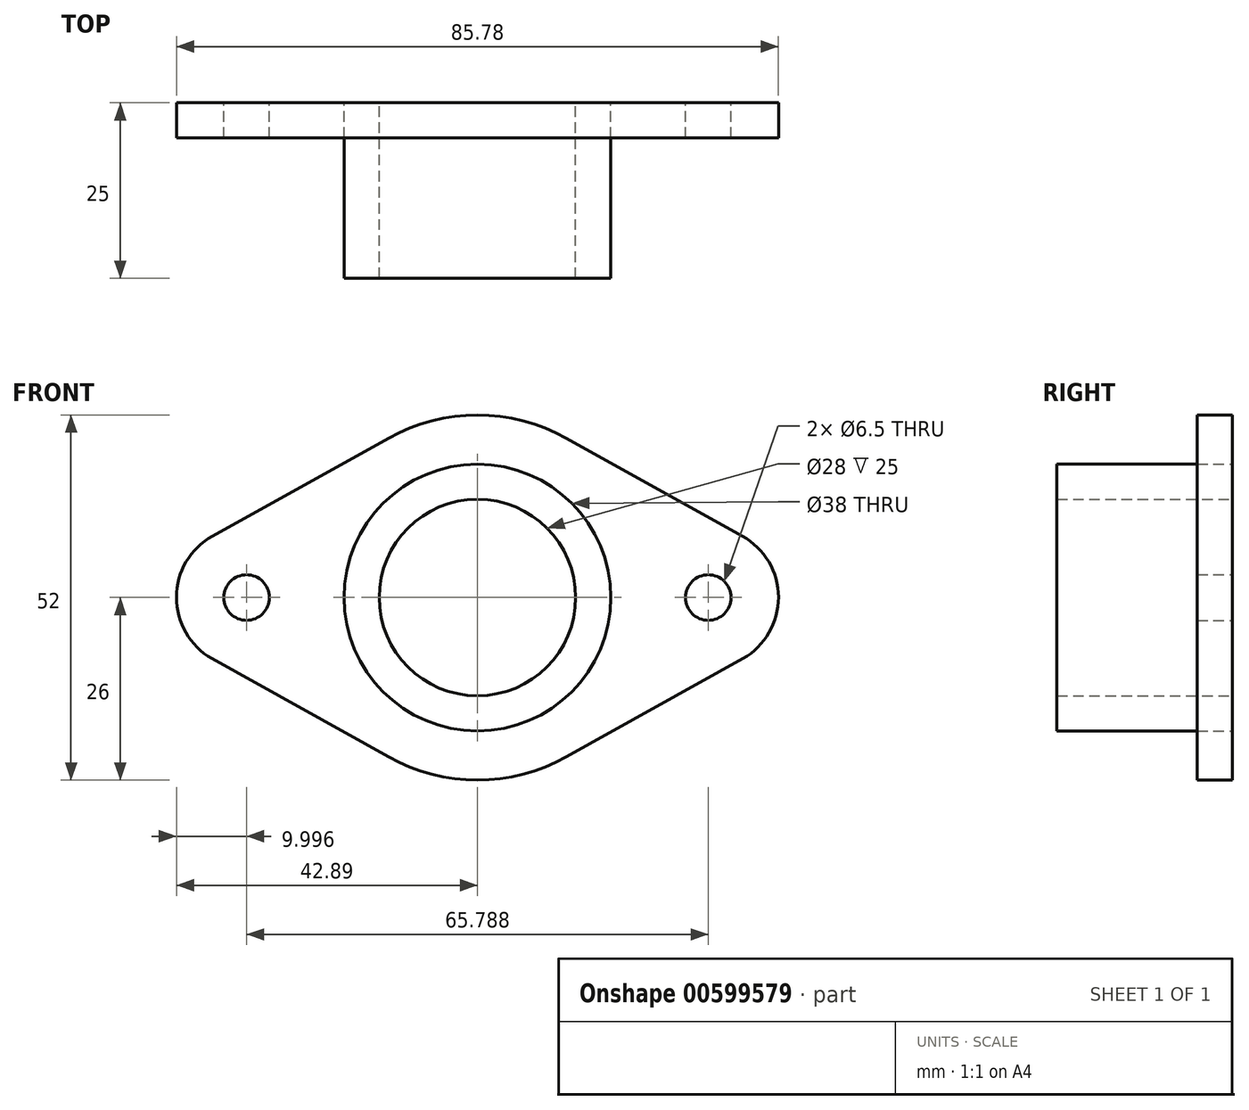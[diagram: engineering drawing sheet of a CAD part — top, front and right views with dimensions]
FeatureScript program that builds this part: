
annotation { "Feature Type Name" : "Feature", "Feature Type Description" : "" }
export const myFeature = defineFeature(function(context is Context, id is Id, definition is map)
    precondition{}
    {
        {
            var Q0;
            Q0=qCreatedBy(makeId("Front.planeOp"),FACE);
            var sketch = newSketch(context, id + "F0", { "sketchPlane" : qUnion([Q0])});
            skArc(sketch, "E0", {"start": v(0, 19) * mm, "mid": v(-19, 0) * mm, "end": v(0, -19) * mm});
            skCircle(sketch, "E1", {"center": v(-32.9, 0) * mm, "radius": 3.25 * mm});
            skLineSegment(sketch, "E2", {"start": v(0, 19) * mm, "end": v(0, 26) * mm});
            skLineSegment(sketch, "E3", {"start": v(0, -19) * mm, "end": v(0, -26) * mm});
            skArc(sketch, "E4", {"start": v(-37.76, 8.74) * mm, "mid": v(-42.9, 0.05) * mm, "end": v(-37.84, -8.7) * mm});
            skArc(sketch, "E5", {"start": v(0, 26) * mm, "mid": v(-6.53, 25.17) * mm, "end": v(-12.65, 22.72) * mm});
            skLineSegment(sketch, "E6", {"start": v(-12.65, 22.72) * mm, "end": v(-37.76, 8.74) * mm});
            skLineSegment(sketch, "E7", {"start": v(-37.84, -8.7) * mm, "end": v(-12.65, -22.72) * mm});
            skArc(sketch, "E8.trimOffspring", {"start": v(-12.65, -22.72) * mm, "mid": v(-6.53, -25.17) * mm, "end": v(0, -26) * mm});
            skLineSegment(sketch, "E9.MirrorCS", {"start": v(37.84, -8.7) * mm, "end": v(12.65, -22.72) * mm});
            skArc(sketch, "E10.MirrorCS", {"start": v(0, 26) * mm, "mid": v(6.53, 25.17) * mm, "end": v(12.65, 22.72) * mm});
            skArc(sketch, "E11.MirrorCS", {"start": v(12.65, -22.72) * mm, "mid": v(6.53, -25.17) * mm, "end": v(0, -26) * mm});
            skArc(sketch, "E12.MirrorCS", {"start": v(0, 19) * mm, "mid": v(19, 0) * mm, "end": v(0, -19) * mm});
            skLineSegment(sketch, "E13.MirrorCS", {"start": v(12.65, 22.72) * mm, "end": v(37.76, 8.74) * mm});
            skArc(sketch, "E14.MirrorCS", {"start": v(37.76, 8.74) * mm, "mid": v(42.9, 0.05) * mm, "end": v(37.84, -8.7) * mm});
            skCircle(sketch, "E15.MirrorC", {"center": v(32.9, 0) * mm, "radius": 3.25 * mm});
            skSolve(sketch);
        }
        {
            var Q0;
            Q0 = qSketchRegion(id + "F0", true);
            extrude(context, id + "F1", {"entities" : qUnion([Q0]), "endBound" : BoundingType.SYMMETRIC, "depth" : 5 * mm, "offsetDistance" : 25 * mm});
        }
        {
            var Q0;
            Q0=makeQuery(id+"F1.opExtrude","CAP_FACE",FACE,{"disambiguationData":[OSD([sQuery(id+"F0.wireOp",EDGE,"E0"),sQuery(id+"F0.wireOp",EDGE,"E1"),sQuery(id+"F0.wireOp",EDGE,"E4"),sQuery(id+"F0.wireOp",EDGE,"E5"),sQuery(id+"F0.wireOp",EDGE,"E6"),sQuery(id+"F0.wireOp",EDGE,"E7"),sQuery(id+"F0.wireOp",EDGE,"E8.trimOffspring"),sQuery(id+"F0.wireOp",EDGE,"E9.MirrorCS"),sQuery(id+"F0.wireOp",EDGE,"E10.MirrorCS"),sQuery(id+"F0.wireOp",EDGE,"E11.MirrorCS"),sQuery(id+"F0.wireOp",EDGE,"E12.MirrorCS"),sQuery(id+"F0.wireOp",EDGE,"E13.MirrorCS"),sQuery(id+"F0.wireOp",EDGE,"E14.MirrorCS"),sQuery(id+"F0.wireOp",EDGE,"E15.MirrorC")])],"isStart":true});
            var sketch = newSketch(context, id + "F2", { "sketchPlane" : qUnion([Q0])});
            skCircle(sketch, "E16", {"center": v(0, 0) * mm, "radius": 14 * mm});
            skCircle(sketch, "E17.0", {"center": v(0, 0) * mm, "radius": 19 * mm});
            skSolve(sketch);
        }
        {
            var Q0;
            Q0 = qSketchRegion(id + "F2", true);
            extrude(context, id + "F3", {"entities" : qUnion([Q0]), "oppositeDirection" : true, "depth" : 25 * mm, "offsetDistance" : 25 * mm});
        }
    });
